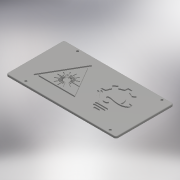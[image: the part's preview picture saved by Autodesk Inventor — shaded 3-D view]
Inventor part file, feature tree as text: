
AUTODESK INVENTOR PART (.ipt)
format: ipt  version: 2017 (Build 210142000, 142)  size: 1,482,752 bytes
history: native  units: mm
features: other x15, sketch x4, extrude x3, fillet x1, hole x1
ambient origin geometry x8: Origin, YZ Plane, XZ Plane, XY Plane, X Axis, Y Axis, Z Axis, Center Point
bodies: Solide2 (feature_tree), Solide1 (feature_tree), Solide9 (feature_tree), Solide10 (feature_tree)
feature tree (24):
  other  "1410-01-01 Partie inferieur.ipt"
  other  "1410-01-03 Logo_fablab.ipt"
  other  "1410-01-04 Logo_laser.ipt"
  extrude  "Extrusion1"  Depth=10.0mm
  fillet  "Congé1"  Radius=5.5mm
  extrude  "Extrusion2"  Depth=2.0mm
  hole  "Perçage1"  [1 undecoded]
  extrude  "Extrusion3"  Depth=2.0mm TaperAngle=0.0deg
  other  "Combiner1"
  other  "Déplacer des corps1"
  other  "Combiner2"
  other  "Déplacer des corps2"
  other  "Combiner3"
  other  "Solide1::1410-01-01 Partie inferieur.ipt"
  other  "FonctionRepérage1"
  sketch  "Esquisse2"
  sketch  "Esquisse3"
  sketch  "Esquisse4"
  sketch  "Esquisse5"
  other  "Solide1::1410-01-03 Logo_fablab.ipt"
  other  "FonctionRepérage3"
  other  "Solide1::1410-01-04 Logo_laser.ipt"
  other  "FonctionRepérage4"
  other  "Projeter les arêtes coupées1"
note: 1 required parameter value undecoded (feature->parameter linkage not recoverable at this tier; creation-order binding heuristic only, values carry confidence <= 0.55)
